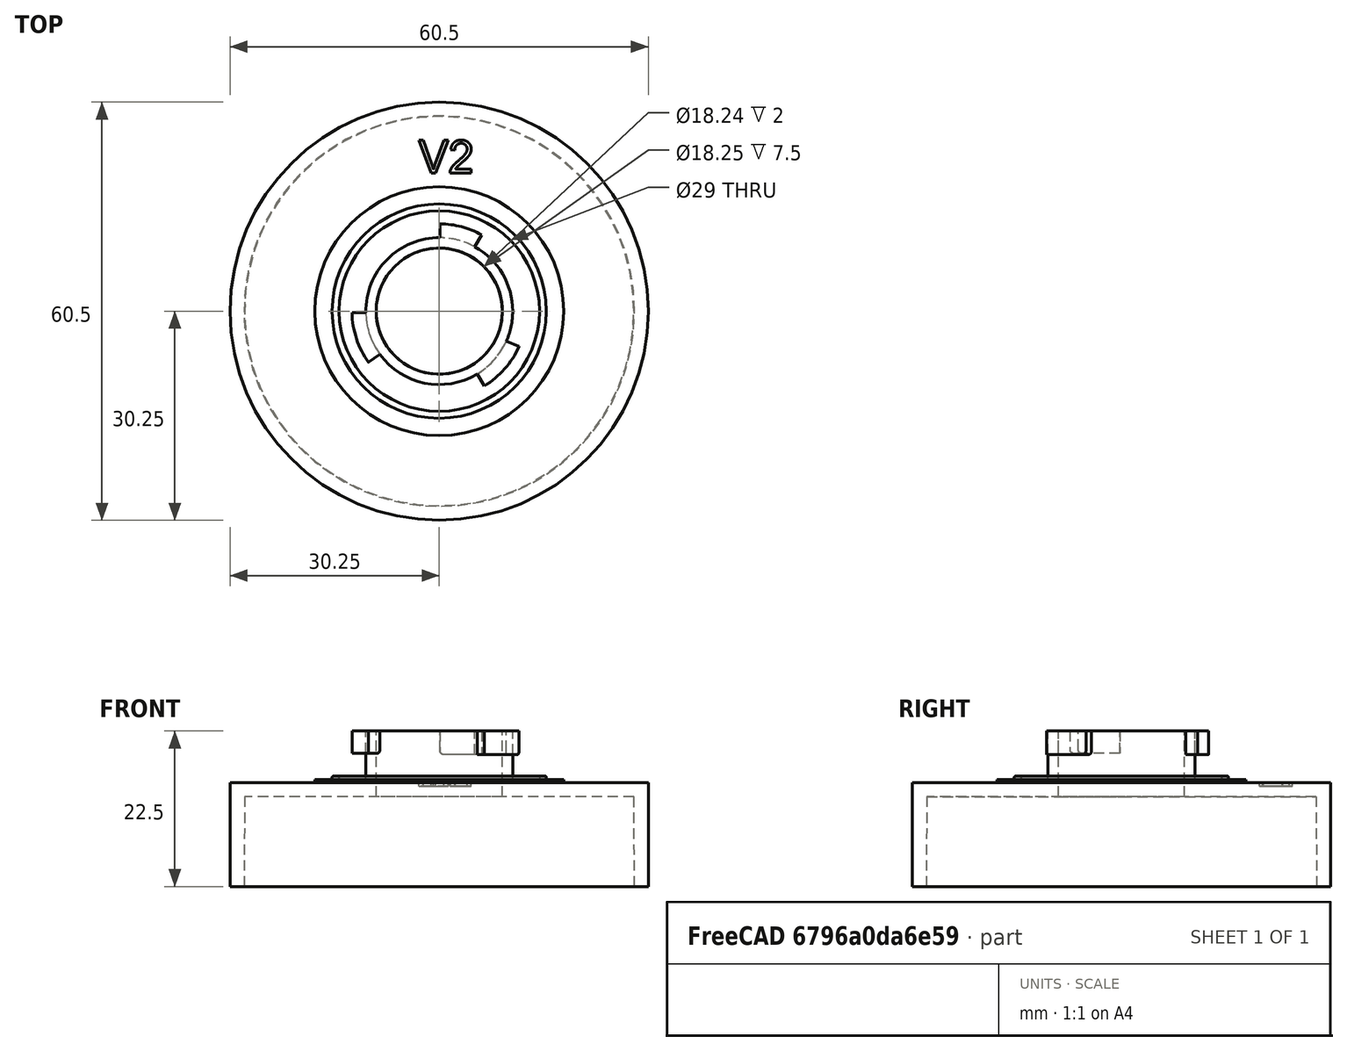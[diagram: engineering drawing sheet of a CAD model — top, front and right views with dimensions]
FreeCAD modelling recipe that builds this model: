
FCSTD DOCUMENT  (FreeCAD 0.18R4 (GitTag))
Label: BlowerInletAdapter-V2
License: All rights reserved
LicenseURL: http://en.wikipedia.org/wiki/All_rights_reserved
objects: Part::Fillet×11, Part::Cylinder×5, Part::Cut×5, Sketcher::SketchObject×4, Part::Revolution×4, Part::MultiFuse×3, Part::Part2DObjectPython×2, Part::Extrusion×2, Part::Cone×1
note: 37 computed .brp shape members not serialized (recipe doc carries the construction recipe); baked Part::Feature solids carry a one-line shape summary decoded from their .brp

FEATURE [Part::Cone] Cone  label="BlowerInlet"
  Angle = 360
  AttacherType = Attacher::AttachEngine3D
  Height = 13
  Radius1 = 28.25
  Radius2 = 28.15
FEATURE [Part::Cylinder] Cylinder  label="OuterBody"
  Angle = 360
  AttacherType = Attacher::AttachEngine3D
  Height = 15
  Radius = 30.25
FEATURE [Part::Cut] Cut  label="OutletCap"
  Base = -> Cylinder
  Tool = -> Cone
FEATURE [Sketcher::SketchObject] Sketch002  label="BayonetTooth001"
  Placement = pos=(0,0,0) rot=(1,0,0;1.5708rad)
  sketch-geometry (4):
    g0: LineSegment StartX=9.125 StartY=8.5 StartZ=0 EndX=12.625 EndY=8.5 EndZ=0
    g1: LineSegment StartX=12.625 StartY=8.5 StartZ=0 EndX=12.625 EndY=5.1 EndZ=0
    g2: LineSegment StartX=12.625 StartY=5.1 StartZ=0 EndX=9.125 EndY=5.1 EndZ=0
    g3: LineSegment StartX=9.125 StartY=5.1 StartZ=0 EndX=9.125 EndY=8.5 EndZ=0
  constraints (12):
    c: Coincident(g0,g1)
    c: Coincident(g1,g2)
    c: Coincident(g2,g3)
    c: Coincident(g3,g0)
    c: Horizontal(g0)
    c: Horizontal(g2)
    c: Vertical(g1)
    c: Vertical(g3)
    c: DistanceY(g1,g0) = 3.4
    c: DistanceX(g2,g1) = 3.5
    c: DistanceY(g-1,g0) = 8.5
    c: DistanceX(g-1,g2) = 9.125
FEATURE [Sketcher::SketchObject] Sketch001  label="BayonetTooth"
  Placement = pos=(0,0,0) rot=(1,0,0;1.5708rad)
  sketch-geometry (4):
    g0: LineSegment StartX=9.125 StartY=8.5 StartZ=0 EndX=12.625 EndY=8.5 EndZ=0
    g1: LineSegment StartX=12.625 StartY=8.5 StartZ=0 EndX=12.625 EndY=5.1 EndZ=0
    g2: LineSegment StartX=12.625 StartY=5.1 StartZ=0 EndX=9.125 EndY=5.1 EndZ=0
    g3: LineSegment StartX=9.125 StartY=5.1 StartZ=0 EndX=9.125 EndY=8.5 EndZ=0
  constraints (12):
    c: Coincident(g0,g1)
    c: Coincident(g1,g2)
    c: Coincident(g2,g3)
    c: Coincident(g3,g0)
    c: Horizontal(g0)
    c: Horizontal(g2)
    c: Vertical(g1)
    c: Vertical(g3)
    c: DistanceY(g1,g0) = 3.4
    c: DistanceX(g2,g1) = 3.5
    c: DistanceY(g-1,g0) = 8.5
    c: DistanceX(g-1,g2) = 9.125
FEATURE [Sketcher::SketchObject] Sketch003  label="BayonetTooth002"
  Placement = pos=(0,0,0) rot=(1,0,0;1.5708rad)
  sketch-geometry (4):
    g0: LineSegment StartX=9.125 StartY=8.5 StartZ=0 EndX=12.625 EndY=8.5 EndZ=0
    g1: LineSegment StartX=12.625 StartY=8.5 StartZ=0 EndX=12.625 EndY=5.3 EndZ=0
    g2: LineSegment StartX=12.625 StartY=5.3 StartZ=0 EndX=9.125 EndY=5.3 EndZ=0
    g3: LineSegment StartX=9.125 StartY=5.3 StartZ=0 EndX=9.125 EndY=8.5 EndZ=0
  constraints (12):
    c: Coincident(g0,g1)
    c: Coincident(g1,g2)
    c: Coincident(g2,g3)
    c: Coincident(g3,g0)
    c: Horizontal(g0)
    c: Horizontal(g2)
    c: Vertical(g1)
    c: Vertical(g3)
    c: DistanceY(g1,g0) = 3.2
    c: DistanceX(g2,g1) = 3.5
    c: DistanceY(g-1,g0) = 8.5
    c: DistanceX(g-1,g2) = 9.125
FEATURE [Sketcher::SketchObject] Sketch  label="GrooveProfile"
  Placement = pos=(0,0,0) rot=(1,0,0;1.5708rad)
  sketch-geometry (4):
    g0: LineSegment StartX=15.5 StartY=2 StartZ=0 EndX=14.5 EndY=2 EndZ=0
    g1: LineSegment StartX=14.5 StartY=2 StartZ=0 EndX=14.5 EndY=1 EndZ=0
    g2: LineSegment StartX=14.5 StartY=1 StartZ=0 EndX=15.5 EndY=1 EndZ=0
    g3: LineSegment StartX=15.5 StartY=1 StartZ=0 EndX=15.5 EndY=2 EndZ=0
  constraints (12):
    c: Coincident(g0,g1)
    c: Coincident(g1,g2)
    c: Coincident(g2,g3)
    c: Coincident(g3,g0)
    c: Horizontal(g0)
    c: Horizontal(g2)
    c: Vertical(g1)
    c: Vertical(g3)
    c: DistanceY(g1,g0) = 1
    c: Equal(g0,g1)
    c: DistanceX(g-1,g0) = 15.5
    c: DistanceY(g1,g-1) = -1
FEATURE [Part::Part2DObjectPython] ShapeString  # Draft 2D object (typed FeaturePython)
  FontFile = <path>
  Size = 5
  String = V2
  Tracking = 0
FEATURE [Part::Cylinder] Cylinder001
  Angle = 360
  AttacherType = Attacher::AttachEngine3D
  Height = 8.5
  Radius = 10.625
FEATURE [Part::Cylinder] Cylinder002
  Angle = 360
  AttacherType = Attacher::AttachEngine3D
  Height = 1.5
  Radius = 18
FEATURE [Part::Extrusion] Extrude
  Base = -> ShapeString
  Dir = (0,0,1)
  DirMode = 2
  FaceMakerClass = Part::FaceMakerBullseye
  LengthFwd = 0.5
  LengthRev = 0
  Placement = pos=(-11,4,0.5) rot=(0.707107,-0.707107,0;3.14159rad)
  Solid = false
  Symmetric = false
FEATURE [Part::Revolution] Revolve003  label="LongTooth2"
  Angle = 35
  Axis = (0,0,1)
  Base = (0,0,0)
  FaceMakerClass = Part::FaceMakerBullseye
  Placement = pos=(0,0,0) rot=(0,0,1;3.15905rad)
  Solid = true
  Source = -> Sketch003
  Symmetric = false
FEATURE [Part::Fillet] Fillet002
  Base = -> Revolve003
  Edges = 1 edges r=0.5: [Edge10]
FEATURE [Part::Fillet] Fillet003
  Base = -> Fillet002
  Edges = 1 edges r=0.5: [Edge8]
FEATURE [Part::Cylinder] Cylinder003
  Angle = 360
  AttacherType = Attacher::AttachEngine3D
  Height = 8.5
  Radius = 9.125
FEATURE [Part::MultiFuse] Fusion
  Shapes = -> [Cylinder002,Cylinder001]
FEATURE [Part::Cut] Cut001
  Base = -> Fusion
  Tool = -> Cylinder003
FEATURE [Part::Fillet] Fillet010
  Base = -> Cut001
  Edges = 1 edges r=0.5: [Edge3]
FEATURE [Part::Cut] Cut002
  Base = -> Fillet010
  Tool = -> Extrude
FEATURE [Part::Revolution] Revolve
  Angle = 360
  Axis = (0,0,1)
  Base = (0,0,0)
  FaceMakerClass = Part::FaceMakerBullseye
  Solid = true
  Source = -> Sketch
  Symmetric = false
FEATURE [Part::Fillet] Fillet
  Base = -> Revolve
  Edges = 1 edges r=0.25: [Edge5]
FEATURE [Part::Fillet] Fillet001
  Base = -> Fillet
  Edges = 1 edges r=0.25: [Edge2]
FEATURE [Part::Fillet] Fillet008
  Base = -> Fillet001
  Edges = 1 edges r=0.25: [Edge10]
FEATURE [Part::Fillet] Fillet009
  Base = -> Fillet008
  Edges = 1 edges r=0.25: [Edge8]
FEATURE [Part::Revolution] Revolve001  label="LongTooth1"
  Angle = 35
  Axis = (0,0,1)
  Base = (0,0,0)
  FaceMakerClass = Part::FaceMakerBullseye
  Placement = pos=(0,0,0) rot=(0,0,-1;1.02974rad)
  Solid = true
  Source = -> Sketch001
  Symmetric = false
FEATURE [Part::Fillet] Fillet006
  Base = -> Revolve001
  Edges = 1 edges r=0.5: [Edge10]
FEATURE [Part::Fillet] Fillet007
  Base = -> Fillet006
  Edges = 1 edges r=0.5: [Edge8]
FEATURE [Part::Revolution] Revolve002  label="ShortTooth"
  Angle = 28.4
  Axis = (0,0,1)
  Base = (0,0,0)
  FaceMakerClass = Part::FaceMakerBullseye
  Placement = pos=(0,0,0) rot=(0,0,1;1.06465rad)
  Solid = true
  Source = -> Sketch002
  Symmetric = false
FEATURE [Part::Fillet] Fillet004
  Base = -> Revolve002
  Edges = 1 edges r=0.5: [Edge10]
FEATURE [Part::Fillet] Fillet005
  Base = -> Fillet004
  Edges = 1 edges r=0.5: [Edge8]
FEATURE [Part::MultiFuse] Fusion001  label="BayonetMtestV2"
  Placement = pos=(0,0,14) rot=(0,0,1;0rad)
  Shapes = -> [Fillet003,Fillet005,Fillet007,Fillet009,Cut002]
FEATURE [Part::Cylinder] Cylinder004  label="Inside"
  Angle = 360
  AttacherType = Attacher::AttachEngine3D
  Height = 10
  Placement = pos=(0,0,13) rot=(0,0,1;0rad)
  Radius = 9.12
FEATURE [Part::MultiFuse] Fusion002  label="Outside"
  Shapes = -> [Cut,Fusion001]
FEATURE [Part::Cut] Cut003  label="BlowerInletAdapterBody"
  Base = -> Fusion002
  Tool = -> Cylinder004
FEATURE [Part::Part2DObjectPython] ShapeString001  # Draft 2D object (typed FeaturePython)
  FontFile = <path>
  Size = 5
  String = V2
  Tracking = 0
FEATURE [Part::Extrusion] Extrude001
  Base = -> ShapeString001
  Dir = (0,0,1)
  DirMode = 2
  FaceMakerClass = Part::FaceMakerBullseye
  LengthFwd = 0.5
  LengthRev = 0
  Placement = pos=(-3,20,14.5) rot=(0,0,1;0rad)
  Solid = false
  Symmetric = false
FEATURE [Part::Cut] Cut004  label="BlowerInletBodyV1"
  Base = -> Cut003
  Tool = -> Extrude001
note: 2 file-system paths scrubbed to <path> (originals preserved in the JSON sidecar)
